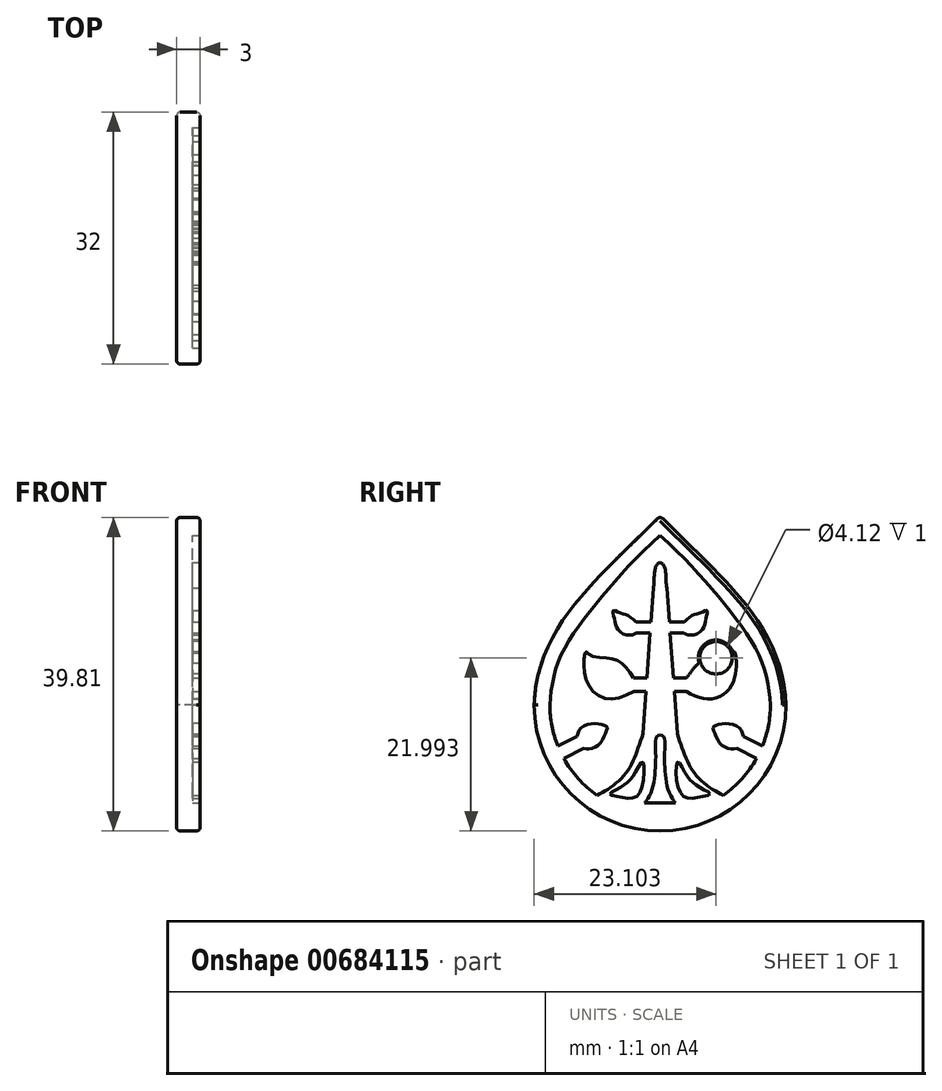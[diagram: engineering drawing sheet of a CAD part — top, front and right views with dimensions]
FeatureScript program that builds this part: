
annotation { "Feature Type Name" : "Feature", "Feature Type Description" : "" }
export const myFeature = defineFeature(function(context is Context, id is Id, definition is map)
    precondition{}
    {
        {
            var Q0;
            Q0=qCreatedBy(makeId("Right.planeOp"),FACE);
            var sketch = newSketch(context, id + "F0", { "sketchPlane" : qUnion([Q0])});
            skArc(sketch, "E0", {"start": v(-16, 0) * mm, "mid": v(-11.31, -11.31) * mm, "end": v(0, -16) * mm});
            skLineSegment(sketch, "E1", {"start": v(0, 24) * mm, "end": v(0, -16) * mm});
            skFitSpline(sketch, "E2", {"points": [v(-16, 0) * mm, v(-12.58, 10.42) * mm, v(0, 24) * mm], "startDerivative": vector(0.62, 24.3) * mm, "endDerivative": vector(26.83, 26.78) * mm});
            skFitSpline(sketch, "E3.MirrorCS", {"points": [v(16, 0) * mm, v(12.58, 10.42) * mm, v(0, 24) * mm], "startDerivative": vector(-0.62, 24.3) * mm, "endDerivative": vector(-26.83, 26.78) * mm});
            skArc(sketch, "E4.MirrorCS", {"start": v(16, 0) * mm, "mid": v(11.31, -11.31) * mm, "end": v(0, -16) * mm});
            skSolve(sketch);
        }
        {
            var Q0;
            Q0 = qSketchRegion(id + "F0", true);
            extrude(context, id + "F1", {"entities" : qUnion([Q0]), "depth" : 3 * mm, "offsetDistance" : 25 * mm});
        }
        {
            var Q0;
            Q0=makeQuery(id+"F1.opExtrude","CAP_FACE",FACE,{"disambiguationData":[OSD([sQuery(id+"F0.wireOp",EDGE,"E0"),sQuery(id+"F0.wireOp",EDGE,"E2"),sQuery(id+"F0.wireOp",EDGE,"E3.MirrorCS"),sQuery(id+"F0.wireOp",EDGE,"E4.MirrorCS")])],"isStart":false});
            var sketch = newSketch(context, id + "F2", { "sketchPlane" : qUnion([Q0])});
            skArc(sketch, "E5", {"start": v(-14, 0) * mm, "mid": v(-13.75, -2.65) * mm, "end": v(-13, -5.2) * mm});
            skFitSpline(sketch, "E6", {"points": [v(-8.03, -11.47) * mm, v(-4.3, -8.6) * mm, v(-2.18, -3.71) * mm], "startDerivative": vector(7.49, 3.5) * mm, "endDerivative": vector(3.65, 10.07) * mm});
            skLineSegment(sketch, "E7", {"start": v(-2.18, -3.71) * mm, "end": v(-1.8, 1.73) * mm});
            skFitSpline(sketch, "E8", {"points": [v(-0.85, 14.83) * mm, v(-0.73, 16.68) * mm, v(0, 18.07) * mm], "startDerivative": vector(0.75, 4.5) * mm, "endDerivative": vector(3.23, 0.04) * mm});
            skLineSegment(sketch, "E9", {"start": v(-13, -5.2) * mm, "end": v(-10.58, -3.97) * mm});
            skLineSegment(sketch, "E10", {"start": v(-12.23, -6.81) * mm, "end": v(-9.74, -5.54) * mm});
            skFitSpline(sketch, "E11", {"points": [v(-10.58, -3.97) * mm, v(-10.08, -2.94) * mm, v(-8.65, -2.38) * mm, v(-7.29, -2.52) * mm, v(-6.73, -2.8) * mm, v(-6.94, -3.57) * mm, v(-7.64, -4.93) * mm, v(-8.76, -5.53) * mm, v(-9.74, -5.54) * mm], "startDerivative": vector(2.56, 8.58) * mm, "endDerivative": vector(-8.2, 0.73) * mm});
            skArc(sketch, "E12.trimOffspring", {"start": v(-12.23, -6.81) * mm, "mid": v(-10.4, -9.38) * mm, "end": v(-8.03, -11.47) * mm});
            skLineSegment(sketch, "E13", {"start": v(-1.16, 10.55) * mm, "end": v(-3.07, 10.55) * mm});
            skLineSegment(sketch, "E14", {"start": v(-1.26, 9.12) * mm, "end": v(-3.02, 9.12) * mm});
            skFitSpline(sketch, "E15", {"points": [v(-3.02, 9.12) * mm, v(-3.56, 8.91) * mm, v(-4.87, 9.12) * mm, v(-5.66, 10.2) * mm, v(-5.86, 11.16) * mm, v(-5.96, 11.97) * mm, v(-5.1, 11.7) * mm, v(-4.18, 11.4) * mm, v(-3.07, 10.55) * mm], "startDerivative": vector(-4.96, -2.95) * mm, "endDerivative": vector(7.76, -8.07) * mm});
            skLineSegment(sketch, "E16", {"start": v(-1.67, 3.42) * mm, "end": v(-3.36, 3.42) * mm});
            skLineSegment(sketch, "E17", {"start": v(-1.8, 1.73) * mm, "end": v(-3.33, 1.73) * mm});
            skLineSegment(sketch, "E18.trimOffspring", {"start": v(-1.16, 10.55) * mm, "end": v(-0.85, 14.83) * mm});
            skLineSegment(sketch, "E19.trimOffspring", {"start": v(-1.67, 3.42) * mm, "end": v(-1.26, 9.12) * mm});
            skFitSpline(sketch, "E20", {"points": [v(-3.36, 3.42) * mm, v(-4.9, 5.28) * mm, v(-6.57, 5.95) * mm, v(-8.98, 6.37) * mm, v(-9.44, 6.75) * mm, v(-9.68, 5.32) * mm, v(-9.05, 2.46) * mm, v(-6.75, 0.78) * mm, v(-3.33, 1.73) * mm], "startDerivative": vector(-11.24, 16.12) * mm, "endDerivative": vector(21.72, 12.64) * mm});
            skFitSpline(sketch, "E21", {"points": [v(-14, 0) * mm, v(-12.83, 5.72) * mm, v(-8.24, 12.73) * mm, v(0, 21.55) * mm], "startDerivative": vector(1.23, 20.3) * mm, "endDerivative": vector(25.1, 22.65) * mm});
            skLineSegment(sketch, "E22", {"start": v(0, 21.55) * mm, "end": v(0, -16) * mm, "construction": true});
            skLineSegment(sketch, "E23.MirrorCS", {"start": v(1.16, 10.55) * mm, "end": v(0.85, 14.83) * mm});
            skFitSpline(sketch, "E24.MirrorCS", {"points": [v(0.85, 14.83) * mm, v(0.73, 16.68) * mm, v(0, 18.07) * mm], "startDerivative": vector(-0.75, 4.5) * mm, "endDerivative": vector(-3.23, 0.04) * mm});
            skFitSpline(sketch, "E25.MirrorCS", {"points": [v(14, 0) * mm, v(12.83, 5.72) * mm, v(8.24, 12.73) * mm, v(0, 21.55) * mm], "startDerivative": vector(-1.23, 20.3) * mm, "endDerivative": vector(-25.1, 22.65) * mm});
            skLineSegment(sketch, "E26.MirrorCS", {"start": v(1.67, 3.42) * mm, "end": v(1.26, 9.12) * mm});
            skLineSegment(sketch, "E27.MirrorCS", {"start": v(1.26, 9.12) * mm, "end": v(3.02, 9.12) * mm});
            skLineSegment(sketch, "E28.MirrorCS", {"start": v(1.16, 10.55) * mm, "end": v(3.07, 10.55) * mm});
            skFitSpline(sketch, "E29.MirrorCS", {"points": [v(3.02, 9.12) * mm, v(3.56, 8.91) * mm, v(4.87, 9.12) * mm, v(5.66, 10.2) * mm, v(5.86, 11.16) * mm, v(5.96, 11.97) * mm, v(5.1, 11.7) * mm, v(4.18, 11.4) * mm, v(3.07, 10.55) * mm], "startDerivative": vector(4.96, -2.95) * mm, "endDerivative": vector(-7.76, -8.07) * mm});
            skFitSpline(sketch, "E30.MirrorCS", {"points": [v(3.36, 3.42) * mm, v(4.9, 5.28) * mm, v(6.57, 5.95) * mm, v(8.98, 6.37) * mm, v(9.44, 6.75) * mm, v(9.68, 5.32) * mm, v(9.05, 2.46) * mm, v(6.75, 0.78) * mm, v(3.33, 1.73) * mm], "startDerivative": vector(11.24, 16.12) * mm, "endDerivative": vector(-21.72, 12.64) * mm});
            skLineSegment(sketch, "E31.MirrorCS", {"start": v(1.67, 3.42) * mm, "end": v(3.36, 3.42) * mm});
            skLineSegment(sketch, "E32.MirrorCS", {"start": v(1.8, 1.73) * mm, "end": v(3.33, 1.73) * mm});
            skLineSegment(sketch, "E33.MirrorCS", {"start": v(2.18, -3.71) * mm, "end": v(1.8, 1.73) * mm});
            skFitSpline(sketch, "E34.MirrorCS", {"points": [v(8.03, -11.47) * mm, v(4.3, -8.6) * mm, v(2.18, -3.71) * mm], "startDerivative": vector(-7.49, 3.5) * mm, "endDerivative": vector(-3.65, 10.07) * mm});
            skArc(sketch, "E35.MirrorCS", {"start": v(12.23, -6.81) * mm, "mid": v(10.4, -9.38) * mm, "end": v(8.03, -11.47) * mm});
            skLineSegment(sketch, "E36.MirrorCS", {"start": v(12.23, -6.81) * mm, "end": v(9.74, -5.54) * mm});
            skLineSegment(sketch, "E37.MirrorCS", {"start": v(13, -5.2) * mm, "end": v(10.58, -3.97) * mm});
            skFitSpline(sketch, "E38.MirrorCS", {"points": [v(10.58, -3.97) * mm, v(10.08, -2.94) * mm, v(8.65, -2.38) * mm, v(7.29, -2.52) * mm, v(6.73, -2.8) * mm, v(6.94, -3.57) * mm, v(7.64, -4.93) * mm, v(8.76, -5.53) * mm, v(9.74, -5.54) * mm], "startDerivative": vector(-2.56, 8.58) * mm, "endDerivative": vector(8.2, 0.73) * mm});
            skArc(sketch, "E39.MirrorCS", {"start": v(14, 0) * mm, "mid": v(13.75, -2.65) * mm, "end": v(13, -5.2) * mm});
            skSolve(sketch);
        }
        {
            var Q0;
            Q0 = qSketchRegion(id + "F2", true);
            extrude(context, id + "F3", {"entities" : qUnion([Q0]), "operationType" : NewBodyOperationType.REMOVE, "oppositeDirection" : true, "depth" : 1 * mm, "offsetDistance" : 25 * mm});
        }
        {
            var Q0;
            Q0=makeQuery(id+"F1.opExtrude","CAP_FACE",FACE,{"disambiguationData":[OSD([sQuery(id+"F0.wireOp",EDGE,"E0"),sQuery(id+"F0.wireOp",EDGE,"E2"),sQuery(id+"F0.wireOp",EDGE,"E3.MirrorCS"),sQuery(id+"F0.wireOp",EDGE,"E4.MirrorCS")])],"isStart":false});
            var sketch = newSketch(context, id + "F4", { "sketchPlane" : qUnion([Q0])});
            skLineSegment(sketch, "E40", {"start": v(0, -12.45) * mm, "end": v(0, -3.8) * mm, "construction": true});
            skFitSpline(sketch, "E41", {"points": [v(0, -3.8) * mm, v(-0.5, -4.11) * mm, v(-0.57, -6.12) * mm, v(-0.64, -8.42) * mm, v(-1.02, -10.76) * mm, v(-1.73, -12.19) * mm, v(-1.96, -12.42) * mm], "startDerivative": vector(-5.27, -1.88) * mm, "endDerivative": vector(-3.84, -1.53) * mm});
            skLineSegment(sketch, "E42", {"start": v(-1.96, -12.42) * mm, "end": v(0, -12.45) * mm});
            skFitSpline(sketch, "E43.MirrorCS", {"points": [v(0, -3.8) * mm, v(0.5, -4.11) * mm, v(0.57, -6.12) * mm, v(0.64, -8.42) * mm, v(1.02, -10.76) * mm, v(1.73, -12.19) * mm, v(1.96, -12.42) * mm], "startDerivative": vector(5.27, -1.88) * mm, "endDerivative": vector(3.84, -1.53) * mm});
            skLineSegment(sketch, "E44.MirrorCS", {"start": v(1.96, -12.42) * mm, "end": v(0, -12.45) * mm});
            skFitSpline(sketch, "E45", {"points": [v(-6.34, -11.31) * mm, v(-5.37, -10.68) * mm, v(-4.16, -9.86) * mm, v(-3.19, -8.7) * mm, v(-2.27, -7.24) * mm, v(-2.1, -9.48) * mm, v(-3.19, -11.74) * mm, v(-5.13, -11.65) * mm, v(-6.34, -11.31) * mm]});
            skFitSpline(sketch, "E46.MirrorC", {"points": [v(6.34, -11.31) * mm, v(5.37, -10.68) * mm, v(4.16, -9.86) * mm, v(3.19, -8.7) * mm, v(2.27, -7.24) * mm, v(2.1, -9.48) * mm, v(3.19, -11.74) * mm, v(5.13, -11.65) * mm, v(6.34, -11.31) * mm]});
            skSolve(sketch);
        }
        {
            var Q0;
            Q0 = qSketchRegion(id + "F4", true);
            extrude(context, id + "F5", {"entities" : qUnion([Q0]), "operationType" : NewBodyOperationType.REMOVE, "oppositeDirection" : true, "depth" : 1 * mm, "offsetDistance" : 25 * mm});
        }
        {
            var Q0;
            Q0=makeQuery(id+"F3.boolean.opBoolean","COPY",FACE,{"derivedFrom":makeQuery(id+"F3.opExtrude","CAP_FACE",FACE,{"disambiguationData":[OSD([sQuery(id+"F2.wireOp",EDGE,"E5"),sQuery(id+"F2.wireOp",EDGE,"E6"),sQuery(id+"F2.wireOp",EDGE,"E7"),sQuery(id+"F2.wireOp",EDGE,"E8"),sQuery(id+"F2.wireOp",EDGE,"E9"),sQuery(id+"F2.wireOp",EDGE,"E10"),sQuery(id+"F2.wireOp",EDGE,"E11"),sQuery(id+"F2.wireOp",EDGE,"E12.trimOffspring"),sQuery(id+"F2.wireOp",EDGE,"E13"),sQuery(id+"F2.wireOp",EDGE,"E14"),sQuery(id+"F2.wireOp",EDGE,"E15"),sQuery(id+"F2.wireOp",EDGE,"E16"),sQuery(id+"F2.wireOp",EDGE,"E17"),sQuery(id+"F2.wireOp",EDGE,"E18.trimOffspring"),sQuery(id+"F2.wireOp",EDGE,"E19.trimOffspring"),sQuery(id+"F2.wireOp",EDGE,"E20"),sQuery(id+"F2.wireOp",EDGE,"12c76496-418e-44f2-832a-2fde6f3aae9b0.MirrorCS"),sQuery(id+"F2.wireOp",EDGE,"467eb0ce-2d8e-41e7-8e2d-113b2440b4de0.MirrorCS"),sQuery(id+"F2.wireOp",EDGE,"c068317f-03a1-49c7-a4f6-c7c69980e16c0.MirrorCS"),sQuery(id+"F2.wireOp",EDGE,"ac8011fb-f518-4cfb-aa67-c64a9f9ae9c00.MirrorCS"),sQuery(id+"F2.wireOp",EDGE,"9baf6e6d-d3ff-49dc-b731-1646830efaab0.MirrorCS"),sQuery(id+"F2.wireOp",EDGE,"5e9949bb-95a8-40fd-a620-21e390203e760.MirrorCS"),sQuery(id+"F2.wireOp",EDGE,"e9188adb-889c-448b-a7b9-5f4749d8fef60.MirrorCS"),sQuery(id+"F2.wireOp",EDGE,"19feb8d4-25cb-4ce1-aa22-d1b968cc36450.MirrorCS"),sQuery(id+"F2.wireOp",EDGE,"52398216-7065-4a0c-a279-c74030393a5d0.MirrorCS"),sQuery(id+"F2.wireOp",EDGE,"071c23d9-b03f-4487-b390-6127d374ac760.MirrorCS"),sQuery(id+"F2.wireOp",EDGE,"3b589403-ec03-46ed-9e03-2d5b77040bab0.MirrorCS"),sQuery(id+"F2.wireOp",EDGE,"61afccf4-8222-4c7e-a894-bbf41ddf23a20.MirrorCS"),sQuery(id+"F2.wireOp",EDGE,"48b6f75e-ee37-4a5c-8801-0af66781d7a50.MirrorCS"),sQuery(id+"F2.wireOp",EDGE,"86858bba-8fb8-44bc-818a-fedaf822c3090.MirrorCS"),sQuery(id+"F2.wireOp",EDGE,"aad8c189-6eea-4b6a-a559-3754407adb040.MirrorCS"),sQuery(id+"F2.wireOp",EDGE,"ac09a47f-3452-481c-b50b-1fca41f53f390.MirrorCS"),sQuery(id+"F2.wireOp",EDGE,"E21"),sQuery(id+"F2.wireOp",EDGE,"f48e4e0d-32f4-4d29-95f7-70098216bb440.MirrorCS")])],"isStart":false})});
            var sketch = newSketch(context, id + "F6", { "sketchPlane" : qUnion([Q0])});
            skSolve(sketch);
        }
        {
            var Q0;
            Q0=makeQuery(id+"F1.opExtrude","CAP_EDGE",EDGE,{"disambiguationData":[OSD([sQuery(id+"F0.wireOp",EDGE,"E2")])],"isStart":false});
            fillet(context, id + "F7", {"entities" : qUnion([Q0]), "radius" : 0.47 * mm, "tangentPropagation" : true, "allowEdgeOverflow" : false});
        }
        {
            var Q0;
            Q0=makeQuery(id+"F1.opExtrude","CAP_EDGE",EDGE,{"disambiguationData":[OSD([sQuery(id+"F0.wireOp",EDGE,"E0"),sQuery(id+"F0.wireOp",EDGE,"E4.MirrorCS")])],"isStart":false});
            var Q1;
            Q1=makeQuery(id+"F1.opExtrude","CAP_EDGE",EDGE,{"disambiguationData":[OSD([sQuery(id+"F0.wireOp",EDGE,"E3.MirrorCS")])],"isStart":false});
            fillet(context, id + "F8", {"entities" : qUnion([Q0, Q1]), "radius" : 0.47 * mm, "tangentPropagation" : true, "allowEdgeOverflow" : false});
        }
        {
            var Q0;
            Q0=makeQuery(id+"F6.imprint","IMPRINT",FACE,{"disambiguationData":[TD([[makeQuery(id+"F6.imprint","IMPRINT",EDGE,{"derivedFrom":makeQuery(id+"F3.boolean.opBoolean","COPY",EDGE,{"derivedFrom":makeQuery(id+"F3.opExtrude","CAP_EDGE",EDGE,{"disambiguationData":[OSD([sQuery(id+"F2.wireOp",EDGE,"E5")])],"isStart":false})})}),1.0]])]});
            var sketch = newSketch(context, id + "F9", { "sketchPlane" : qUnion([Q0])});
            skCircle(sketch, "E47", {"center": v(7.1, 6) * mm, "radius": 2.25 * mm});
            skSolve(sketch);
        }
        {
            var Q0;
            Q0 = qSketchRegion(id + "F9", true);
            extrude(context, id + "F10", {"entities" : qUnion([Q0]), "operationType" : NewBodyOperationType.REMOVE, "depth" : 1 * mm, "offsetDistance" : 25 * mm});
        }
        {
            var Q0;
            Q0=makeQuery(id+"F6.imprint","IMPRINT",FACE,{"disambiguationData":[TD([[makeQuery(id+"F6.imprint","IMPRINT",EDGE,{"derivedFrom":makeQuery(id+"F3.boolean.opBoolean","COPY",EDGE,{"derivedFrom":makeQuery(id+"F3.opExtrude","CAP_EDGE",EDGE,{"disambiguationData":[OSD([sQuery(id+"F2.wireOp",EDGE,"E5")])],"isStart":false})})}),1.0]])]});
            var sketch = newSketch(context, id + "F11", { "sketchPlane" : qUnion([Q0])});
            skCircle(sketch, "E48", {"center": v(7.1, 6) * mm, "radius": 2.25 * mm});
            skCircle(sketch, "E49", {"center": v(7.1, 6) * mm, "radius": 2.06 * mm});
            skSolve(sketch);
        }
        {
            var Q0;
            Q0 = qSketchRegion(id + "F11", true);
            extrude(context, id + "F12", {"entities" : qUnion([Q0]), "operationType" : NewBodyOperationType.ADD, "depth" : 1 * mm, "offsetDistance" : 25 * mm});
        }
        {
            var Q0;
            Q0=makeQuery(id+"F1.opExtrude","CAP_EDGE",EDGE,{"disambiguationData":[OSD([sQuery(id+"F0.wireOp",EDGE,"E0"),sQuery(id+"F0.wireOp",EDGE,"E4.MirrorCS")])],"isStart":true});
            var Q1;
            Q1=makeQuery(id+"F1.opExtrude","CAP_EDGE",EDGE,{"disambiguationData":[OSD([sQuery(id+"F0.wireOp",EDGE,"E3.MirrorCS")])],"isStart":true});
            var Q2;
            Q2=makeQuery(id+"F1.opExtrude","CAP_EDGE",EDGE,{"disambiguationData":[OSD([sQuery(id+"F0.wireOp",EDGE,"E2")])],"isStart":true});
            fillet(context, id + "F13", {"entities" : qUnion([Q0, Q1, Q2]), "radius" : 0.47 * mm, "tangentPropagation" : true, "allowEdgeOverflow" : false});
        }
    });
